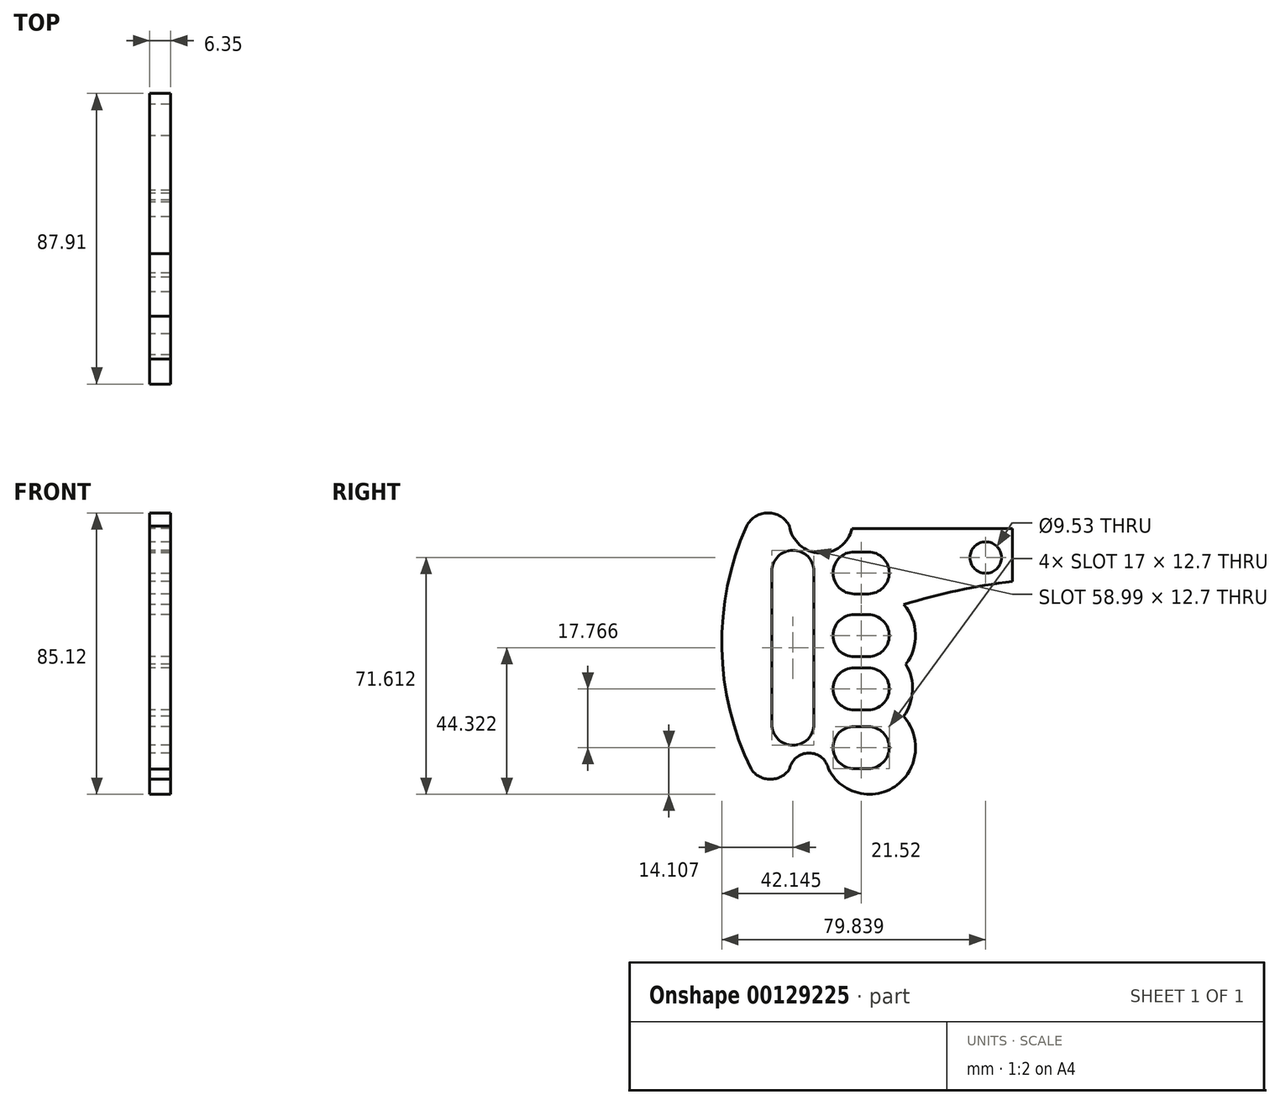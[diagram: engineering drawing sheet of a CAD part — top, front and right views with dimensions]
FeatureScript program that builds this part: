
annotation { "Feature Type Name" : "Feature", "Feature Type Description" : "" }
export const myFeature = defineFeature(function(context is Context, id is Id, definition is map)
    precondition{}
    {
        {
            var Q0;
            Q0=qCreatedBy(makeId("Right.planeOp"),FACE);
            var sketch = newSketch(context, id + "F0", { "sketchPlane" : qUnion([Q0])});
            skArc(sketch, "E0", {"start": v(-24.8, 23.83) * mm, "mid": v(-32.3, -13.15) * mm, "end": v(-23.42, -49.82) * mm});
            skArc(sketch, "E1", {"start": v(-11.85, 23.83) * mm, "mid": v(-18.33, 27.75) * mm, "end": v(-24.8, 23.83) * mm});
            skArc(sketch, "E2", {"start": v(-11.85, 23.83) * mm, "mid": v(-5.77, 16.24) * mm, "end": v(3.84, 17.78) * mm});
            skArc(sketch, "E3", {"start": v(3.84, 17.78) * mm, "mid": v(5.91, 20.14) * mm, "end": v(7.12, 23.04) * mm});
            skLineSegment(sketch, "E4", {"start": v(7.12, 23.04) * mm, "end": v(55.6, 23.04) * mm});
            skLineSegment(sketch, "E5", {"start": v(55.6, 23.04) * mm, "end": v(55.6, 7) * mm});
            skArc(sketch, "E6", {"start": v(55.6, 7) * mm, "mid": v(39.01, 4.25) * mm, "end": v(22.75, 0) * mm});
            skArc(sketch, "E7", {"start": v(-23.42, -49.82) * mm, "mid": v(-17.63, -52.85) * mm, "end": v(-11.85, -49.82) * mm});
            skLineSegment(sketch, "E8", {"start": v(7.68, 9.6) * mm, "end": v(11.97, 9.6) * mm, "construction": true});
            skLineSegment(sketch, "E9", {"start": v(7.68, -9.4) * mm, "end": v(11.97, -9.4) * mm, "construction": true});
            skLineSegment(sketch, "E10", {"start": v(7.68, -43.26) * mm, "end": v(11.97, -43.26) * mm, "construction": true});
            skLineSegment(sketch, "E11", {"start": v(7.68, -25.5) * mm, "end": v(11.97, -25.5) * mm, "construction": true});
            skArc(sketch, "E12.0.startCap", {"start": v(7.68, 3.26) * mm, "mid": v(1.33, 9.6) * mm, "end": v(7.68, 15.96) * mm});
            skArc(sketch, "E12.0.endCap", {"start": v(11.97, 15.96) * mm, "mid": v(18.32, 9.6) * mm, "end": v(11.97, 3.26) * mm});
            skLineSegment(sketch, "E12.0.left", {"start": v(7.68, 15.96) * mm, "end": v(11.97, 15.96) * mm});
            skLineSegment(sketch, "E12.0.right", {"start": v(7.68, 3.26) * mm, "end": v(11.97, 3.26) * mm});
            skArc(sketch, "E12.1.startCap", {"start": v(7.68, -15.75) * mm, "mid": v(1.33, -9.4) * mm, "end": v(7.68, -3.05) * mm});
            skArc(sketch, "E12.1.endCap", {"start": v(11.97, -3.05) * mm, "mid": v(18.32, -9.4) * mm, "end": v(11.97, -15.75) * mm});
            skLineSegment(sketch, "E12.1.left", {"start": v(7.68, -3.05) * mm, "end": v(11.97, -3.05) * mm});
            skLineSegment(sketch, "E12.1.right", {"start": v(7.68, -15.75) * mm, "end": v(11.97, -15.75) * mm});
            skArc(sketch, "E12.2.startCap", {"start": v(7.68, -49.61) * mm, "mid": v(1.33, -43.26) * mm, "end": v(7.68, -36.91) * mm});
            skArc(sketch, "E12.2.endCap", {"start": v(11.97, -36.91) * mm, "mid": v(18.32, -43.26) * mm, "end": v(11.97, -49.61) * mm});
            skLineSegment(sketch, "E12.2.left", {"start": v(7.68, -36.91) * mm, "end": v(11.97, -36.91) * mm});
            skLineSegment(sketch, "E12.2.right", {"start": v(7.68, -49.61) * mm, "end": v(11.97, -49.61) * mm});
            skArc(sketch, "E12.3.startCap", {"start": v(7.68, -31.85) * mm, "mid": v(1.33, -25.5) * mm, "end": v(7.68, -19.15) * mm});
            skArc(sketch, "E12.3.endCap", {"start": v(11.97, -19.15) * mm, "mid": v(18.32, -25.5) * mm, "end": v(11.97, -31.85) * mm});
            skLineSegment(sketch, "E12.3.left", {"start": v(7.68, -19.15) * mm, "end": v(11.97, -19.15) * mm});
            skLineSegment(sketch, "E12.3.right", {"start": v(7.68, -31.85) * mm, "end": v(11.97, -31.85) * mm});
            skArc(sketch, "E13.0", {"start": v(22.69, -33.8) * mm, "mid": v(26.24, -42.34) * mm, "end": v(23.82, -51.27) * mm});
            skArc(sketch, "E14.trimOffspring", {"start": v(22.75, 0) * mm, "mid": v(26.26, -8.92) * mm, "end": v(23.35, -18.06) * mm});
            skArc(sketch, "E15.trimOffspring", {"start": v(23.35, -18.06) * mm, "mid": v(25.38, -26.03) * mm, "end": v(22.69, -33.8) * mm});
            skArc(sketch, "E16", {"start": v(0, -49.82) * mm, "mid": v(-5.92, -44.92) * mm, "end": v(-11.85, -49.82) * mm});
            skArc(sketch, "E17", {"start": v(0, -49.82) * mm, "mid": v(11.5, -57.34) * mm, "end": v(23.82, -51.27) * mm});
            skLineSegment(sketch, "E18", {"start": v(-10.8, 10.1) * mm, "end": v(-10.8, -36.2) * mm, "construction": true});
            skArc(sketch, "E19.0.startCap", {"start": v(-17.15, 10.1) * mm, "mid": v(-10.8, 16.45) * mm, "end": v(-4.45, 10.1) * mm});
            skArc(sketch, "E19.0.endCap", {"start": v(-4.45, -36.2) * mm, "mid": v(-10.8, -42.54) * mm, "end": v(-17.15, -36.2) * mm});
            skLineSegment(sketch, "E19.0.left", {"start": v(-4.45, 10.1) * mm, "end": v(-4.45, -36.2) * mm});
            skLineSegment(sketch, "E19.0.right", {"start": v(-17.15, 10.1) * mm, "end": v(-17.15, -36.2) * mm});
            skCircle(sketch, "E20", {"center": v(47.52, 14.24) * mm, "radius": 4.76 * mm});
            skSolve(sketch);
        }
        {
            var Q0;
            Q0 = qSketchRegion(id + "F0", true);
            extrude(context, id + "F1", {"entities" : qUnion([Q0]), "depth" : 6.35 * mm});
        }
    });
